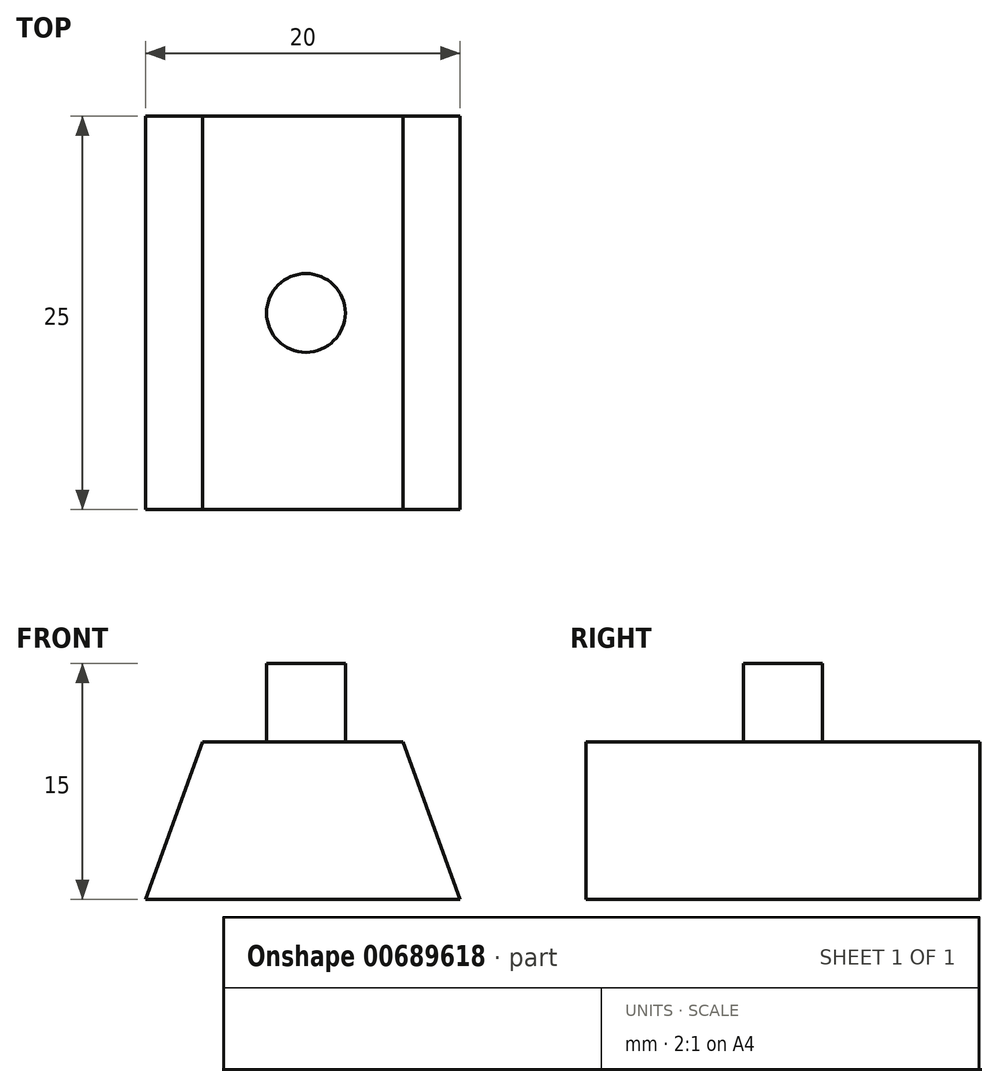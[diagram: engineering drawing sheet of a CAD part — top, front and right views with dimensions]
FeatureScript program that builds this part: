
annotation { "Feature Type Name" : "Feature", "Feature Type Description" : "" }
export const myFeature = defineFeature(function(context is Context, id is Id, definition is map)
    precondition{}
    {
        {
            var Q0;
            Q0=qCreatedBy(makeId("Front.planeOp"),FACE);
            var sketch = newSketch(context, id + "F0", { "sketchPlane" : qUnion([Q0])});
            skLineSegment(sketch, "E0", {"start": v(0, 0) * mm, "end": v(20, 0) * mm});
            skLineSegment(sketch, "E1", {"start": v(3.64, 10) * mm, "end": v(0, 0) * mm});
            skLineSegment(sketch, "E2", {"start": v(16.36, 10) * mm, "end": v(20, 0) * mm});
            skLineSegment(sketch, "E3", {"start": v(3.64, 10) * mm, "end": v(16.36, 10) * mm});
            skSolve(sketch);
        }
        {
            var Q0;
            Q0=makeQuery(id+"F0.imprint","IMPRINT",FACE,{"disambiguationData":[TD([[makeQuery(id+"F0.imprint","IMPRINT",EDGE,{"derivedFrom":sQuery(id+"F0.wireOp",EDGE,"E0")}),1.0]])]});
            extrude(context, id + "F1", {"entities" : qUnion([Q0]), "depth" : 25 * mm, "offsetDistance" : 25 * mm});
        }
        {
            var Q0;
            Q0=qCreatedBy(makeId("Top.planeOp"),FACE);
            var sketch = newSketch(context, id + "F2", { "sketchPlane" : qUnion([Q0])});
            skCircle(sketch, "E4", {"center": v(10.2, -12.5) * mm, "radius": 2.5 * mm});
            skSolve(sketch);
        }
        {
            var Q0;
            Q0=makeQuery(id+"F2.imprint","IMPRINT",FACE,{"disambiguationData":[TD([[makeQuery(id+"F2.imprint","IMPRINT",EDGE,{"derivedFrom":sQuery(id+"F2.wireOp",EDGE,"E4")}),1.0]])]});
            var Q1;
            Q1=sQuery(id+"F2.wireOp",EDGE,"E4");
            extrude(context, id + "F3", {"entities" : qUnion([Q0]), "operationType" : NewBodyOperationType.ADD, "surfaceEntities" : qUnion([Q1]), "depth" : 15 * mm, "offsetDistance" : 25 * mm});
        }
    });
